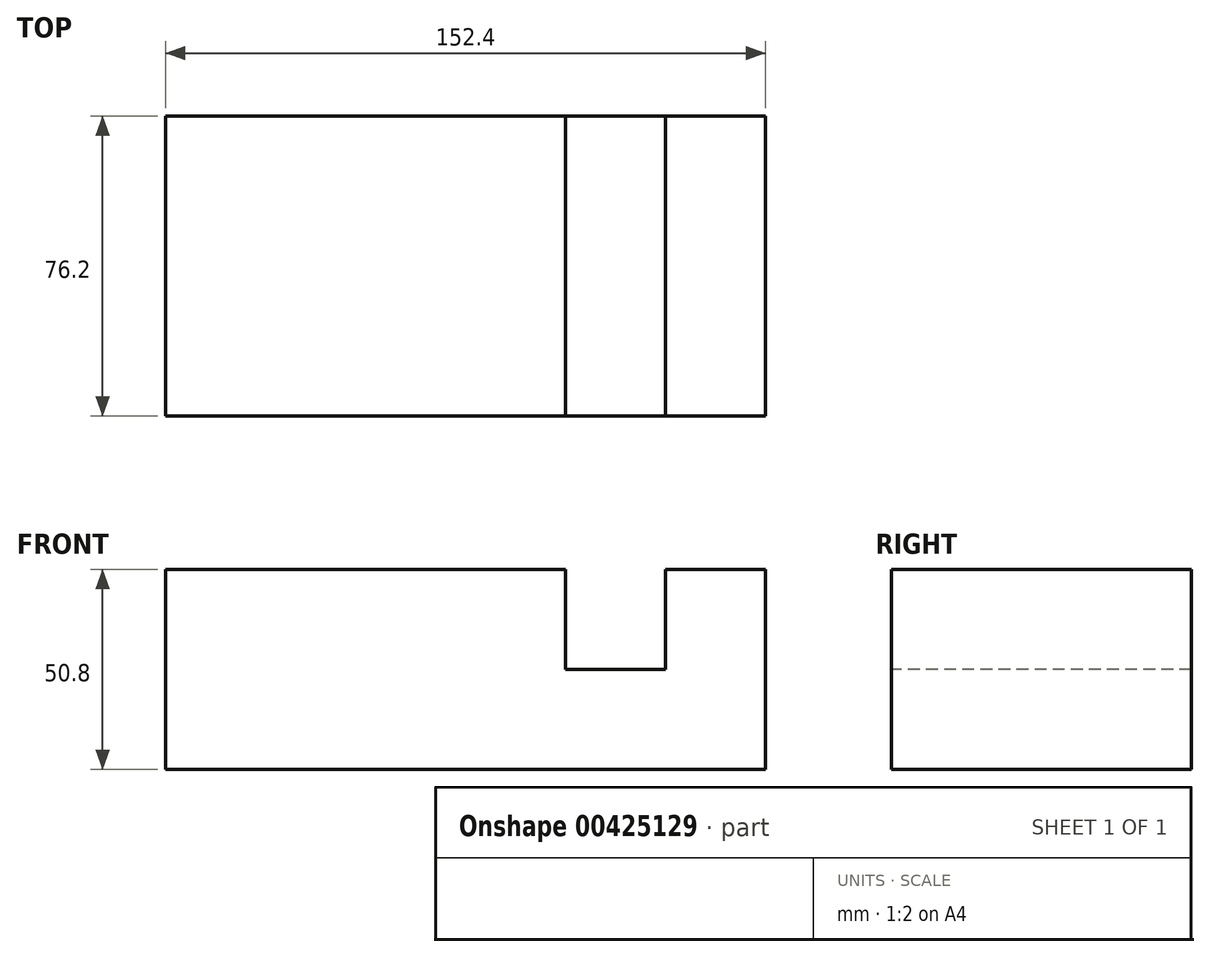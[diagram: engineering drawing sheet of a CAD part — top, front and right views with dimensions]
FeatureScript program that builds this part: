
annotation { "Feature Type Name" : "Feature", "Feature Type Description" : "" }
export const myFeature = defineFeature(function(context is Context, id is Id, definition is map)
    precondition{}
    {
        {
            var Q0;
            Q0=qCreatedBy(makeId("Front.planeOp"),FACE);
            var sketch = newSketch(context, id + "F0", { "sketchPlane" : qUnion([Q0])});
            skLineSegment(sketch, "E0", {"start": v(0, 0) * mm, "end": v(152.4, 0) * mm});
            skLineSegment(sketch, "E1", {"start": v(152.4, 0) * mm, "end": v(152.4, 50.8) * mm});
            skLineSegment(sketch, "E2", {"start": v(152.4, 50.8) * mm, "end": v(0, 50.8) * mm});
            skLineSegment(sketch, "E3", {"start": v(0, 50.8) * mm, "end": v(0, -3.33) * mm});
            skSolve(sketch);
        }
        {
            var Q0;
            {var subQ0=sQuery(id+"F0.wireOp",EDGE,"E0");Q0=makeQuery(id+"F0.imprint","IMPRINT",FACE,{"disambiguationData":[TD([[makeQuery(id+"F0.imprint","IMPRINT",EDGE,{"derivedFrom":subQ0}),1.0]])]});}
            extrude(context, id + "F1", {"entities" : qUnion([Q0]), "depth" : 76.2 * mm});
        }
        {
            var Q0;
            Q0=makeQuery(id+"F1.opExtrude","CAP_FACE",FACE,{"disambiguationData":[OSD([sQuery(id+"F0.wireOp",EDGE,"E0"),sQuery(id+"F0.wireOp",EDGE,"E1"),sQuery(id+"F0.wireOp",EDGE,"E2"),sQuery(id+"F0.wireOp",EDGE,"E3")])],"isStart":false});
            var sketch = newSketch(context, id + "F2", { "sketchPlane" : qUnion([Q0])});
            skLineSegment(sketch, "E4", {"start": v(152.4, 50.8) * mm, "end": v(127, 50.8) * mm});
            skLineSegment(sketch, "E5", {"start": v(127, 50.8) * mm, "end": v(127, 25.4) * mm});
            skLineSegment(sketch, "E6", {"start": v(127, 25.4) * mm, "end": v(101.6, 25.4) * mm});
            skLineSegment(sketch, "E7", {"start": v(101.6, 25.4) * mm, "end": v(101.6, 50.8) * mm});
            skLineSegment(sketch, "E8", {"start": v(101.6, 50.8) * mm, "end": v(127, 50.8) * mm});
            skSolve(sketch);
        }
        {
            var Q0;
            Q0=makeQuery(id+"F2.imprint","IMPRINT",FACE,{"disambiguationData":[TD([[makeQuery(id+"F2.imprint","IMPRINT",EDGE,{"derivedFrom":sQuery(id+"F2.wireOp",EDGE,"E5")}),-1.0]])]});
            extrude(context, id + "F3", {"entities" : qUnion([Q0]), "operationType" : NewBodyOperationType.REMOVE, "oppositeDirection" : true, "depth" : 76.2 * mm});
        }
    });
